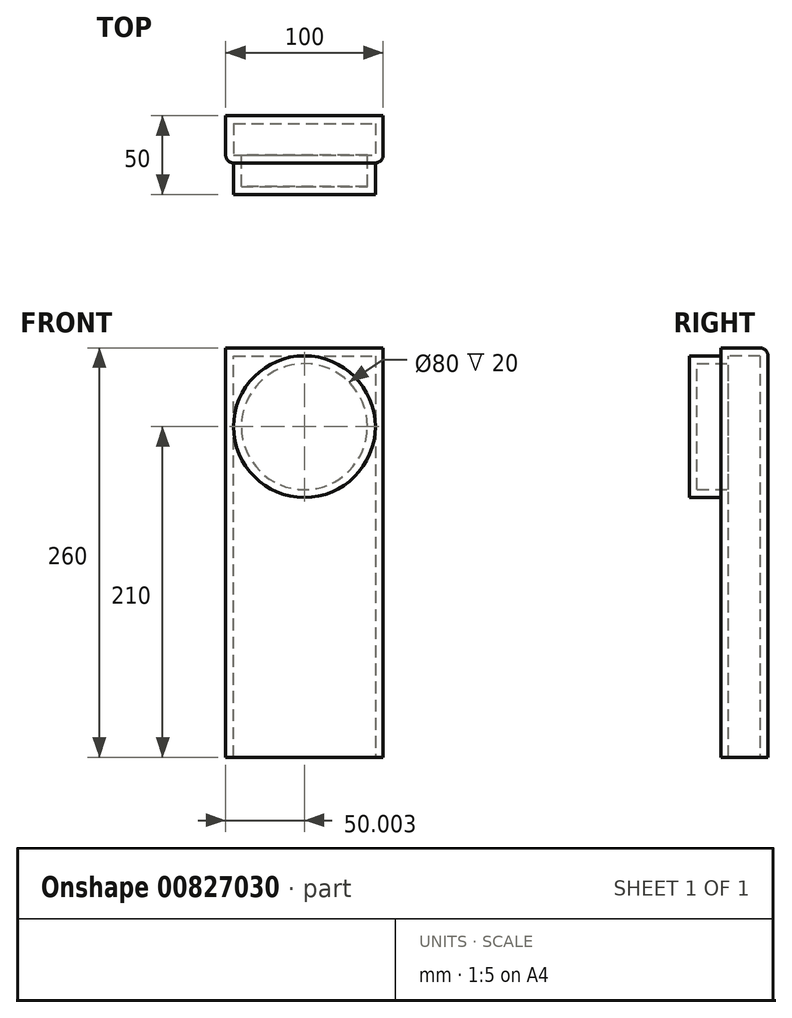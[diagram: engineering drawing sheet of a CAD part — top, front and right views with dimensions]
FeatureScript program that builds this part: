
annotation { "Feature Type Name" : "Feature", "Feature Type Description" : "" }
export const myFeature = defineFeature(function(context is Context, id is Id, definition is map)
    precondition{}
    {
        {
            var Q0;
            Q0=qCreatedBy(makeId("Front.planeOp"),FACE);
            var sketch = newSketch(context, id + "F0", { "sketchPlane" : qUnion([Q0])});
            skLineSegment(sketch, "E0.bottom", {"start": v(-50.19, 100) * mm, "end": v(49.81, 100) * mm});
            skLineSegment(sketch, "E0.top", {"start": v(-50.19, -160) * mm, "end": v(49.81, -160) * mm});
            skLineSegment(sketch, "E0.left", {"start": v(-50.19, 100) * mm, "end": v(-50.19, -160) * mm});
            skLineSegment(sketch, "E0.right", {"start": v(49.81, 100) * mm, "end": v(49.81, -160) * mm});
            skSolve(sketch);
        }
        {
            var Q0;
            Q0=makeQuery(id+"F0.imprint","IMPRINT",FACE,{"disambiguationData":[TD([[makeQuery(id+"F0.imprint","IMPRINT",EDGE,{"derivedFrom":sQuery(id+"F0.wireOp",EDGE,"E0.bottom")}),-1.0]])]});
            extrude(context, id + "F1", {"entities" : qUnion([Q0]), "oppositeDirection" : true, "depth" : 30 * mm, "offsetDistance" : 25 * mm});
        }
        {
            var Q0;
            Q0=qCreatedBy(makeId("Front.planeOp"),FACE);
            var sketch = newSketch(context, id + "F2", { "sketchPlane" : qUnion([Q0])});
            skCircle(sketch, "E1", {"center": v(-0.19, 50) * mm, "radius": 45 * mm});
            skSolve(sketch);
        }
        {
            var Q0;
            Q0=makeQuery(id+"FDgpK6pD7PDtTYR_1.opExtrude","SWEPT_EDGE",EDGE,{"disambiguationData":[OSD([sQuery(id+"F2.wireOp",EDGE,"Aa3zQbE1-5aUb-0iAw-HSvo-nNrJyn6XvE0x.bottom"),sQuery(id+"F2.wireOp",EDGE,"Aa3zQbE1-5aUb-0iAw-HSvo-nNrJyn6XvE0x.left")])]});
            var Q1;
            Q1=makeQuery(id+"FDgpK6pD7PDtTYR_1.opExtrude","SWEPT_EDGE",EDGE,{"disambiguationData":[OSD([sQuery(id+"F2.wireOp",EDGE,"Aa3zQbE1-5aUb-0iAw-HSvo-nNrJyn6XvE0x.bottom"),sQuery(id+"F2.wireOp",EDGE,"Aa3zQbE1-5aUb-0iAw-HSvo-nNrJyn6XvE0x.right")])]});
            var Q2;
            Q2=makeQuery(id+"FDgpK6pD7PDtTYR_1.opExtrude","SWEPT_EDGE",EDGE,{"disambiguationData":[OSD([sQuery(id+"F2.wireOp",EDGE,"Aa3zQbE1-5aUb-0iAw-HSvo-nNrJyn6XvE0x.top"),sQuery(id+"F2.wireOp",EDGE,"Aa3zQbE1-5aUb-0iAw-HSvo-nNrJyn6XvE0x.right")])]});
            var Q3;
            Q3=makeQuery(id+"FDgpK6pD7PDtTYR_1.opExtrude","SWEPT_EDGE",EDGE,{"disambiguationData":[OSD([sQuery(id+"F2.wireOp",EDGE,"Aa3zQbE1-5aUb-0iAw-HSvo-nNrJyn6XvE0x.top"),sQuery(id+"F2.wireOp",EDGE,"Aa3zQbE1-5aUb-0iAw-HSvo-nNrJyn6XvE0x.left")])]});
            var Q4;
            Q4=makeQuery(id+"F1.opExtrude","CAP_EDGE",EDGE,{"disambiguationData":[OSD([sQuery(id+"F0.wireOp",EDGE,"E0.right")])],"isStart":true});
            var Q5;
            Q5=makeQuery(id+"F1.opExtrude","CAP_EDGE",EDGE,{"disambiguationData":[OSD([sQuery(id+"F0.wireOp",EDGE,"E0.left")])],"isStart":true});
            var Q6;
            Q6=makeQuery(id+"F1.opExtrude","CAP_EDGE",EDGE,{"disambiguationData":[OSD([sQuery(id+"F0.wireOp",EDGE,"E0.bottom")])],"isStart":false});
            fillet(context, id + "F3", {"entities" : qUnion([Q0, Q1, Q2, Q3, Q4, Q5, Q6]), "radius" : 5 * mm, "tangentPropagation" : true, "allowEdgeOverflow" : false});
        }
        {
            var Q0;
            Q0=makeQuery(id+"F2.imprint","IMPRINT",FACE,{"disambiguationData":[TD([[makeQuery(id+"F2.imprint","IMPRINT",EDGE,{"derivedFrom":sQuery(id+"F2.wireOp",EDGE,"E1")}),1.0]])]});
            extrude(context, id + "F4", {"entities" : qUnion([Q0]), "operationType" : NewBodyOperationType.ADD, "depth" : 20 * mm, "offsetDistance" : 25 * mm});
        }
        {
            var Q0;
            Q0=makeQuery(id+"F1.opExtrude","SWEPT_FACE",FACE,{"disambiguationData":[OSD([sQuery(id+"F0.wireOp",EDGE,"E0.top")])]});
            shell(context, id + "F5", {"entities" : qUnion([Q0]), "thickness" : 5 * mm});
        }
    });
